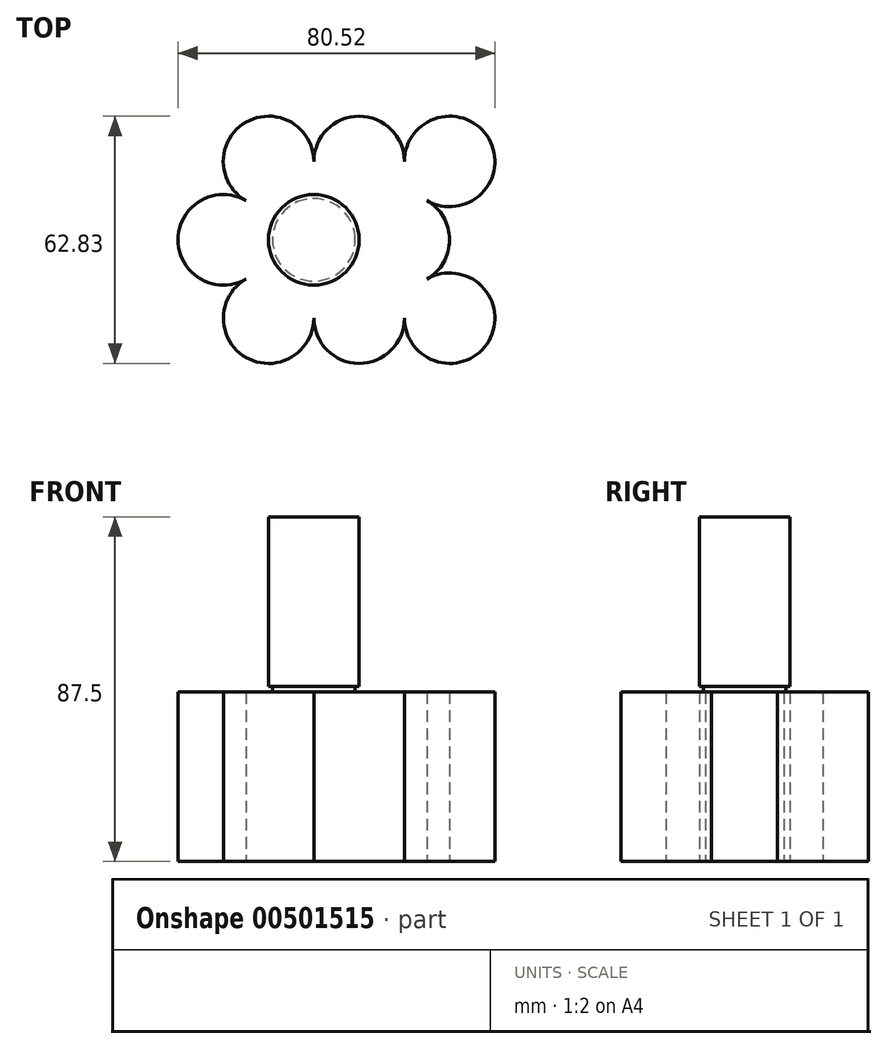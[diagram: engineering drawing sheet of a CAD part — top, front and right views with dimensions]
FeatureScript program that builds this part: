
annotation { "Feature Type Name" : "Feature", "Feature Type Description" : "" }
export const myFeature = defineFeature(function(context is Context, id is Id, definition is map)
    precondition{}
    {
        {
            var Q0;
            Q0=qCreatedBy(makeId("Top.planeOp"),FACE);
            var sketch = newSketch(context, id + "F0", { "sketchPlane" : qUnion([Q0])});
            skCircle(sketch, "E0", {"center": v(16.05, 0) * mm, "radius": 11.5 * mm});
            skPoint(sketch, "E1.first.point", {"position": v(27.55, 0) * mm});
            skCircle(sketch, "E2", {"center": v(39.05, 0) * mm, "radius": 11.5 * mm, "construction": true});
            skPoint(sketch, "E2.second.point", {"position": v(50.55, 0) * mm});
            skPoint(sketch, "E2.third.point", {"position": v(38.48, 11.49) * mm});
            skCircle(sketch, "E3", {"center": v(27.55, 19.92) * mm, "radius": 11.5 * mm});
            skPoint(sketch, "E3.first.point", {"position": v(21.8, 9.96) * mm});
            skPoint(sketch, "E3.second.point", {"position": v(33.3, 9.96) * mm});
            skPoint(sketch, "E3.third.point", {"position": v(23.6, 30.71) * mm});
            skCircle(sketch, "E4", {"center": v(27.57, -19.91) * mm, "radius": 11.5 * mm});
            skPoint(sketch, "E4.first.point", {"position": v(21.8, -9.96) * mm});
            skPoint(sketch, "E4.second.point", {"position": v(33.65, -10.15) * mm});
            skPoint(sketch, "E4.third.point", {"position": v(32.49, -30.3) * mm});
            skCircle(sketch, "E5.1.0.0", {"center": v(50.55, 19.92) * mm, "radius": 11.5 * mm});
            skCircle(sketch, "E5.1.0.1", {"center": v(39.05, 0) * mm, "radius": 11.5 * mm});
            skCircle(sketch, "E5.1.0.2", {"center": v(50.57, -19.91) * mm, "radius": 11.5 * mm});
            skCircle(sketch, "E5.2.0.0", {"center": v(73.55, 19.92) * mm, "radius": 11.5 * mm});
            skCircle(sketch, "E5.2.0.1", {"center": v(62.05, 0) * mm, "radius": 11.5 * mm});
            skCircle(sketch, "E5.2.0.2", {"center": v(73.57, -19.91) * mm, "radius": 11.5 * mm});
            skLineSegment(sketch, "E5.direction1", {"start": v(27.55, 19.92) * mm, "end": v(50.55, 19.92) * mm, "construction": true});
            skSolve(sketch);
        }
        {
            var Q0;
            Q0=qCreatedBy(makeId("Top.planeOp"),FACE);
            var sketch = newSketch(context, id + "F1", { "sketchPlane" : qUnion([Q0])});
            skCircle(sketch, "E6.0", {"center": v(27.55, 19.92) * mm, "radius": 11.5 * mm});
            skCircle(sketch, "E6.1", {"center": v(16.05, 0) * mm, "radius": 11.5 * mm});
            skCircle(sketch, "E6.2", {"center": v(27.57, -19.91) * mm, "radius": 11.5 * mm});
            skCircle(sketch, "E6.3", {"center": v(50.55, 19.92) * mm, "radius": 11.5 * mm});
            skCircle(sketch, "E6.4", {"center": v(39.05, 0) * mm, "radius": 11.5 * mm});
            skCircle(sketch, "E6.5", {"center": v(50.57, -19.91) * mm, "radius": 11.5 * mm});
            skCircle(sketch, "E6.6", {"center": v(73.55, 19.92) * mm, "radius": 11.5 * mm});
            skCircle(sketch, "E6.7", {"center": v(62.05, 0) * mm, "radius": 11.5 * mm});
            skCircle(sketch, "E6.8", {"center": v(73.57, -19.91) * mm, "radius": 11.5 * mm});
            skLineSegment(sketch, "E6.9", {"start": v(27.55, 19.92) * mm, "end": v(50.55, 19.92) * mm});
            skCircle(sketch, "E6.10", {"center": v(39.05, 0) * mm, "radius": 11.5 * mm});
            skSolve(sketch);
        }
        {
            var Q0;
            {var subQ0=sQuery(id+"F1.wireOp",EDGE,"E6.6");var subQ1=makeQuery(id+"F1.imprint","INTERSECT",VERTEX,{"derivedFrom":[sQuery(id+"F1.wireOp",EDGE,"E6.3"),subQ0]});Q0=makeQuery(id+"F1.imprint","IMPRINT",FACE,{"disambiguationData":[TD([[makeQuery(id+"F1.imprint","IMPRINT",EDGE,{"disambiguationData":[TD([[subQ1,-1.0]])],"derivedFrom":subQ0}),1.0]])]});}
            var Q1;
            {var subQ0=sQuery(id+"F1.wireOp",EDGE,"E6.8");var subQ1=makeQuery(id+"F1.imprint","INTERSECT",VERTEX,{"derivedFrom":[sQuery(id+"F1.wireOp",EDGE,"E6.5"),subQ0]});Q1=makeQuery(id+"F1.imprint","IMPRINT",FACE,{"disambiguationData":[TD([[makeQuery(id+"F1.imprint","IMPRINT",EDGE,{"disambiguationData":[TD([[subQ1,1.0]])],"derivedFrom":subQ0}),1.0]])]});}
            var Q2;
            {var subQ0=sQuery(id+"F1.wireOp",EDGE,"E6.0");var subQ1=makeQuery(id+"F1.imprint","INTERSECT",VERTEX,{"derivedFrom":[subQ0,sQuery(id+"F1.wireOp",EDGE,"E6.1")]});Q2=makeQuery(id+"F1.imprint","IMPRINT",FACE,{"disambiguationData":[TD([[makeQuery(id+"F1.imprint","IMPRINT",EDGE,{"disambiguationData":[TD([[subQ1,1.0]])],"derivedFrom":subQ0}),1.0]])]});}
            var Q3;
            {var subQ0=sQuery(id+"F1.wireOp",EDGE,"E6.1");var subQ1=makeQuery(id+"F1.imprint","INTERSECT",VERTEX,{"derivedFrom":[sQuery(id+"F1.wireOp",EDGE,"E6.0"),subQ0]});Q3=makeQuery(id+"F1.imprint","IMPRINT",FACE,{"disambiguationData":[TD([[makeQuery(id+"F1.imprint","IMPRINT",EDGE,{"disambiguationData":[TD([[subQ1,1.0]])],"derivedFrom":subQ0}),1.0]])]});}
            var Q4;
            {var subQ0=sQuery(id+"F1.wireOp",EDGE,"E6.1");var subQ1=sQuery(id+"F1.wireOp",EDGE,"E6.0");var subQ2=makeQuery(id+"F1.imprint","INTERSECT",VERTEX,{"derivedFrom":[subQ1,subQ0]});Q4=makeQuery(id+"F1.imprint","IMPRINT",FACE,{"disambiguationData":[TD([[makeQuery(id+"F1.imprint","IMPRINT",EDGE,{"disambiguationData":[TD([[subQ2,-1.0]])],"derivedFrom":subQ1}),-1.0]])]});}
            var Q5;
            {var subQ0=sQuery(id+"F1.wireOp",EDGE,"E6.3");var subQ1=sQuery(id+"F1.wireOp",EDGE,"E6.0");var subQ2=makeQuery(id+"F1.imprint","INTERSECT",VERTEX,{"derivedFrom":[subQ1,subQ0]});Q5=makeQuery(id+"F1.imprint","IMPRINT",FACE,{"disambiguationData":[TD([[makeQuery(id+"F1.imprint","IMPRINT",EDGE,{"disambiguationData":[TD([[subQ2,1.0]])],"derivedFrom":subQ1}),-1.0]])]});}
            var Q6;
            {var subQ0=sQuery(id+"F1.wireOp",EDGE,"E6.2");var subQ1=sQuery(id+"F1.wireOp",EDGE,"E6.1");var subQ2=makeQuery(id+"F1.imprint","INTERSECT",VERTEX,{"derivedFrom":[subQ1,subQ0]});Q6=makeQuery(id+"F1.imprint","IMPRINT",FACE,{"disambiguationData":[TD([[makeQuery(id+"F1.imprint","IMPRINT",EDGE,{"disambiguationData":[TD([[subQ2,-1.0]])],"derivedFrom":subQ1}),-1.0]])]});}
            var Q7;
            {var subQ0=sQuery(id+"F1.wireOp",EDGE,"E6.2");var subQ1=makeQuery(id+"F1.imprint","INTERSECT",VERTEX,{"derivedFrom":[subQ0,sQuery(id+"F1.wireOp",EDGE,"E6.5")]});Q7=makeQuery(id+"F1.imprint","IMPRINT",FACE,{"disambiguationData":[TD([[makeQuery(id+"F1.imprint","IMPRINT",EDGE,{"disambiguationData":[TD([[subQ1,-1.0]])],"derivedFrom":subQ0}),1.0]])]});}
            var Q8;
            {var subQ0=sQuery(id+"F1.wireOp",EDGE,"E6.5");var subQ1=sQuery(id+"F1.wireOp",EDGE,"E6.2");var subQ2=makeQuery(id+"F1.imprint","INTERSECT",VERTEX,{"derivedFrom":[subQ1,subQ0]});Q8=makeQuery(id+"F1.imprint","IMPRINT",FACE,{"disambiguationData":[TD([[makeQuery(id+"F1.imprint","IMPRINT",EDGE,{"disambiguationData":[TD([[subQ2,-1.0]])],"derivedFrom":subQ1}),-1.0]])]});}
            var Q9;
            {var subQ0=sQuery(id+"F1.wireOp",EDGE,"E6.3");var subQ1=makeQuery(id+"F1.imprint","INTERSECT",VERTEX,{"derivedFrom":[sQuery(id+"F1.wireOp",EDGE,"E6.0"),subQ0]});Q9=makeQuery(id+"F1.imprint","IMPRINT",FACE,{"disambiguationData":[TD([[makeQuery(id+"F1.imprint","IMPRINT",EDGE,{"disambiguationData":[TD([[subQ1,1.0]])],"derivedFrom":subQ0}),1.0]])]});}
            var Q10;
            {var subQ0=sQuery(id+"F1.wireOp",EDGE,"E6.6");var subQ1=sQuery(id+"F1.wireOp",EDGE,"E6.3");var subQ2=makeQuery(id+"F1.imprint","INTERSECT",VERTEX,{"derivedFrom":[subQ1,subQ0]});Q10=makeQuery(id+"F1.imprint","IMPRINT",FACE,{"disambiguationData":[TD([[makeQuery(id+"F1.imprint","IMPRINT",EDGE,{"disambiguationData":[TD([[subQ2,1.0]])],"derivedFrom":subQ1}),-1.0]])]});}
            var Q11;
            {var subQ0=sQuery(id+"F1.wireOp",EDGE,"E6.8");var subQ1=sQuery(id+"F1.wireOp",EDGE,"E6.5");var subQ2=makeQuery(id+"F1.imprint","INTERSECT",VERTEX,{"derivedFrom":[subQ1,subQ0]});Q11=makeQuery(id+"F1.imprint","IMPRINT",FACE,{"disambiguationData":[TD([[makeQuery(id+"F1.imprint","IMPRINT",EDGE,{"disambiguationData":[TD([[subQ2,-1.0]])],"derivedFrom":subQ1}),-1.0]])]});}
            var Q12;
            {var subQ0=sQuery(id+"F1.wireOp",EDGE,"E6.5");var subQ2=makeQuery(id+"F1.imprint","INTERSECT",VERTEX,{"derivedFrom":[subQ0,sQuery(id+"F1.wireOp",EDGE,"E6.8")]});Q12=makeQuery(id+"F1.imprint","IMPRINT",FACE,{"disambiguationData":[TD([[makeQuery(id+"F1.imprint","IMPRINT",EDGE,{"disambiguationData":[TD([[subQ2,-1.0]])],"derivedFrom":subQ0}),1.0]])]});}
            var Q13;
            {var subQ0=sQuery(id+"F1.wireOp",EDGE,"E6.7");var subQ1=sQuery(id+"F1.wireOp",EDGE,"E6.5");var subQ6=makeQuery(id+"F1.imprint","INTERSECT",VERTEX,{"disambiguationData":[OD(0.0)],"derivedFrom":[subQ1,subQ0]});Q13=makeQuery(id+"F1.imprint","IMPRINT",FACE,{"disambiguationData":[TD([[makeQuery(id+"F1.imprint","IMPRINT",EDGE,{"disambiguationData":[TD([[subQ6,-1.0]])],"derivedFrom":subQ1}),-1.0]])]});}
            var Q14;
            {var subQ0=sQuery(id+"F0.wireOp",EDGE,"E5.1.0.1");var subQ5=sQuery(id+"F0.wireOp",EDGE,"E4");var subQ6=makeQuery(id+"F0.imprint","INTERSECT",VERTEX,{"disambiguationData":[OD(0.0)],"derivedFrom":[subQ5,subQ0]});Q14=makeQuery(id+"F0.imprint","IMPRINT",FACE,{"disambiguationData":[TD([[makeQuery(id+"F0.imprint","IMPRINT",EDGE,{"disambiguationData":[TD([[subQ6,-1.0]])],"derivedFrom":subQ5}),-1.0]])]});}
            var Q15;
            {var subQ0=sQuery(id+"F0.wireOp",EDGE,"E5.2.0.2");var subQ1=sQuery(id+"F0.wireOp",EDGE,"E5.1.0.2");var subQ2=makeQuery(id+"F0.imprint","INTERSECT",VERTEX,{"derivedFrom":[subQ1,subQ0]});Q15=makeQuery(id+"F0.imprint","IMPRINT",FACE,{"disambiguationData":[TD([[makeQuery(id+"F0.imprint","IMPRINT",EDGE,{"disambiguationData":[TD([[subQ2,-1.0]])],"derivedFrom":subQ1}),-1.0]])]});}
            var Q16;
            {var subQ0=sQuery(id+"F0.wireOp",EDGE,"E5.2.0.0");var subQ1=sQuery(id+"F0.wireOp",EDGE,"E5.1.0.0");var subQ2=makeQuery(id+"F0.imprint","INTERSECT",VERTEX,{"derivedFrom":[subQ1,subQ0]});Q16=makeQuery(id+"F0.imprint","IMPRINT",FACE,{"disambiguationData":[TD([[makeQuery(id+"F0.imprint","IMPRINT",EDGE,{"disambiguationData":[TD([[subQ2,1.0]])],"derivedFrom":subQ1}),-1.0]])]});}
            var Q17;
            {var subQ0=sQuery(id+"F0.wireOp",EDGE,"E5.1.0.2");var subQ2=makeQuery(id+"F0.imprint","INTERSECT",VERTEX,{"derivedFrom":[subQ0,sQuery(id+"F0.wireOp",EDGE,"E5.2.0.2")]});Q17=makeQuery(id+"F0.imprint","IMPRINT",FACE,{"disambiguationData":[TD([[makeQuery(id+"F0.imprint","IMPRINT",EDGE,{"disambiguationData":[TD([[subQ2,-1.0]])],"derivedFrom":subQ0}),1.0]])]});}
            var Q18;
            {var subQ0=sQuery(id+"F0.wireOp",EDGE,"E5.2.0.1");var subQ2=sQuery(id+"F0.wireOp",EDGE,"E5.1.0.2");var subQ6=makeQuery(id+"F0.imprint","INTERSECT",VERTEX,{"disambiguationData":[OD(0.0)],"derivedFrom":[subQ2,subQ0]});Q18=makeQuery(id+"F0.imprint","IMPRINT",FACE,{"disambiguationData":[TD([[makeQuery(id+"F0.imprint","IMPRINT",EDGE,{"disambiguationData":[TD([[subQ6,-1.0]])],"derivedFrom":subQ2}),-1.0]])]});}
            var Q19;
            {var subQ0=sQuery(id+"F0.wireOp",EDGE,"E5.2.0.1");var subQ1=sQuery(id+"F0.wireOp",EDGE,"E5.1.0.1");var subQ2=makeQuery(id+"F0.imprint","INTERSECT",VERTEX,{"derivedFrom":[subQ1,subQ0]});Q19=makeQuery(id+"F0.imprint","IMPRINT",FACE,{"disambiguationData":[TD([[makeQuery(id+"F0.imprint","IMPRINT",EDGE,{"disambiguationData":[TD([[subQ2,1.0]])],"derivedFrom":subQ1}),-1.0]])]});}
            var Q20;
            {var subQ0=sQuery(id+"F0.wireOp",EDGE,"E5.2.0.0");var subQ1=makeQuery(id+"F0.imprint","INTERSECT",VERTEX,{"derivedFrom":[sQuery(id+"F0.wireOp",EDGE,"E5.1.0.0"),subQ0]});Q20=makeQuery(id+"F0.imprint","IMPRINT",FACE,{"disambiguationData":[TD([[makeQuery(id+"F0.imprint","IMPRINT",EDGE,{"disambiguationData":[TD([[subQ1,-1.0]])],"derivedFrom":subQ0}),1.0]])]});}
            var Q21;
            {var subQ0=sQuery(id+"F0.wireOp",EDGE,"E5.2.0.2");var subQ1=makeQuery(id+"F0.imprint","INTERSECT",VERTEX,{"derivedFrom":[sQuery(id+"F0.wireOp",EDGE,"E5.1.0.2"),subQ0]});Q21=makeQuery(id+"F0.imprint","IMPRINT",FACE,{"disambiguationData":[TD([[makeQuery(id+"F0.imprint","IMPRINT",EDGE,{"disambiguationData":[TD([[subQ1,1.0]])],"derivedFrom":subQ0}),1.0]])]});}
            var Q22;
            {var subQ0=sQuery(id+"F0.wireOp",EDGE,"E0");var subQ1=makeQuery(id+"F0.imprint","INTERSECT",VERTEX,{"derivedFrom":[subQ0,sQuery(id+"F0.wireOp",EDGE,"E3")]});Q22=makeQuery(id+"F0.imprint","IMPRINT",FACE,{"disambiguationData":[TD([[makeQuery(id+"F0.imprint","IMPRINT",EDGE,{"disambiguationData":[TD([[subQ1,1.0]])],"derivedFrom":subQ0}),1.0]])]});}
            var Q23;
            {var subQ0=sQuery(id+"F0.wireOp",EDGE,"E3");var subQ1=makeQuery(id+"F0.imprint","INTERSECT",VERTEX,{"derivedFrom":[sQuery(id+"F0.wireOp",EDGE,"E0"),subQ0]});Q23=makeQuery(id+"F0.imprint","IMPRINT",FACE,{"disambiguationData":[TD([[makeQuery(id+"F0.imprint","IMPRINT",EDGE,{"disambiguationData":[TD([[subQ1,1.0]])],"derivedFrom":subQ0}),1.0]])]});}
            var Q24;
            {var subQ0=sQuery(id+"F0.wireOp",EDGE,"E3");var subQ1=sQuery(id+"F0.wireOp",EDGE,"E0");var subQ2=makeQuery(id+"F0.imprint","INTERSECT",VERTEX,{"derivedFrom":[subQ1,subQ0]});Q24=makeQuery(id+"F0.imprint","IMPRINT",FACE,{"disambiguationData":[TD([[makeQuery(id+"F0.imprint","IMPRINT",EDGE,{"disambiguationData":[TD([[subQ2,1.0]])],"derivedFrom":subQ1}),-1.0]])]});}
            var Q25;
            {var subQ0=sQuery(id+"F0.wireOp",EDGE,"E4");var subQ1=sQuery(id+"F0.wireOp",EDGE,"E0");var subQ2=makeQuery(id+"F0.imprint","INTERSECT",VERTEX,{"derivedFrom":[subQ1,subQ0]});Q25=makeQuery(id+"F0.imprint","IMPRINT",FACE,{"disambiguationData":[TD([[makeQuery(id+"F0.imprint","IMPRINT",EDGE,{"disambiguationData":[TD([[subQ2,-1.0]])],"derivedFrom":subQ1}),-1.0]])]});}
            var Q26;
            {var subQ0=sQuery(id+"F0.wireOp",EDGE,"E5.1.0.0");var subQ1=sQuery(id+"F0.wireOp",EDGE,"E3");var subQ2=makeQuery(id+"F0.imprint","INTERSECT",VERTEX,{"derivedFrom":[subQ1,subQ0]});Q26=makeQuery(id+"F0.imprint","IMPRINT",FACE,{"disambiguationData":[TD([[makeQuery(id+"F0.imprint","IMPRINT",EDGE,{"disambiguationData":[TD([[subQ2,1.0]])],"derivedFrom":subQ1}),-1.0]])]});}
            var Q27;
            {var subQ0=sQuery(id+"F0.wireOp",EDGE,"E4");var subQ1=makeQuery(id+"F0.imprint","INTERSECT",VERTEX,{"derivedFrom":[subQ0,sQuery(id+"F0.wireOp",EDGE,"E5.1.0.2")]});Q27=makeQuery(id+"F0.imprint","IMPRINT",FACE,{"disambiguationData":[TD([[makeQuery(id+"F0.imprint","IMPRINT",EDGE,{"disambiguationData":[TD([[subQ1,-1.0]])],"derivedFrom":subQ0}),1.0]])]});}
            var Q28;
            {var subQ0=sQuery(id+"F0.wireOp",EDGE,"E5.1.0.2");var subQ1=sQuery(id+"F0.wireOp",EDGE,"E4");var subQ2=makeQuery(id+"F0.imprint","INTERSECT",VERTEX,{"derivedFrom":[subQ1,subQ0]});Q28=makeQuery(id+"F0.imprint","IMPRINT",FACE,{"disambiguationData":[TD([[makeQuery(id+"F0.imprint","IMPRINT",EDGE,{"disambiguationData":[TD([[subQ2,-1.0]])],"derivedFrom":subQ1}),-1.0]])]});}
            var Q29;
            {var subQ0=sQuery(id+"F0.wireOp",EDGE,"E5.1.0.0");var subQ1=makeQuery(id+"F0.imprint","INTERSECT",VERTEX,{"derivedFrom":[sQuery(id+"F0.wireOp",EDGE,"E3"),subQ0]});Q29=makeQuery(id+"F0.imprint","IMPRINT",FACE,{"disambiguationData":[TD([[makeQuery(id+"F0.imprint","IMPRINT",EDGE,{"disambiguationData":[TD([[subQ1,1.0]])],"derivedFrom":subQ0}),1.0]])]});}
            var Q30;
            {var subQ0=sQuery(id+"F0.wireOp",EDGE,"E5.1.0.1");var subQ1=sQuery(id+"F0.wireOp",EDGE,"E5.1.0.0");var subQ2=makeQuery(id+"F0.imprint","INTERSECT",VERTEX,{"derivedFrom":[subQ1,subQ0]});Q30=makeQuery(id+"F0.imprint","IMPRINT",FACE,{"disambiguationData":[TD([[makeQuery(id+"F0.imprint","IMPRINT",EDGE,{"disambiguationData":[TD([[subQ2,-1.0]])],"derivedFrom":subQ1}),-1.0]])]});}
            var Q31;
            {var subQ0=sQuery(id+"F1.wireOp",EDGE,"E6.10");var subQ5=sQuery(id+"F1.wireOp",EDGE,"E6.2");var subQ6=makeQuery(id+"F1.imprint","INTERSECT",VERTEX,{"disambiguationData":[OD(0.0)],"derivedFrom":[subQ5,subQ0]});Q31=makeQuery(id+"F1.imprint","IMPRINT",FACE,{"disambiguationData":[TD([[makeQuery(id+"F1.imprint","IMPRINT",EDGE,{"disambiguationData":[TD([[subQ6,-1.0]])],"derivedFrom":subQ5}),-1.0]])]});}
            var Q32;
            {var subQ0=sQuery(id+"F1.wireOp",EDGE,"E6.10");var subQ1=sQuery(id+"F1.wireOp",EDGE,"E6.3");var subQ2=makeQuery(id+"F1.imprint","INTERSECT",VERTEX,{"derivedFrom":[subQ1,subQ0]});Q32=makeQuery(id+"F1.imprint","IMPRINT",FACE,{"disambiguationData":[TD([[makeQuery(id+"F1.imprint","IMPRINT",EDGE,{"disambiguationData":[TD([[subQ2,-1.0]])],"derivedFrom":subQ1}),-1.0]])]});}
            var Q33;
            {var subQ0=sQuery(id+"F1.wireOp",EDGE,"E6.7");var subQ1=sQuery(id+"F1.wireOp",EDGE,"E6.5");var subQ2=makeQuery(id+"F1.imprint","INTERSECT",VERTEX,{"disambiguationData":[OD(1.0)],"derivedFrom":[subQ1,subQ0]});Q33=makeQuery(id+"F1.imprint","IMPRINT",FACE,{"disambiguationData":[TD([[makeQuery(id+"F1.imprint","IMPRINT",EDGE,{"disambiguationData":[TD([[subQ2,-1.0]])],"derivedFrom":subQ1}),-1.0]])]});}
            var Q34;
            {var subQ0=sQuery(id+"F0.wireOp",EDGE,"E5.2.0.1");var subQ1=sQuery(id+"F0.wireOp",EDGE,"E5.1.0.2");var subQ2=makeQuery(id+"F0.imprint","INTERSECT",VERTEX,{"disambiguationData":[OD(0.0)],"derivedFrom":[subQ1,subQ0]});Q34=makeQuery(id+"F0.imprint","IMPRINT",FACE,{"disambiguationData":[TD([[makeQuery(id+"F0.imprint","IMPRINT",EDGE,{"disambiguationData":[TD([[subQ2,-1.0]])],"derivedFrom":subQ1}),1.0]])]});}
            var Q35;
            {var subQ0=sQuery(id+"F1.wireOp",EDGE,"E6.7");var subQ1=sQuery(id+"F1.wireOp",EDGE,"E6.5");var subQ2=makeQuery(id+"F1.imprint","INTERSECT",VERTEX,{"disambiguationData":[OD(0.0)],"derivedFrom":[subQ1,subQ0]});Q35=makeQuery(id+"F1.imprint","IMPRINT",FACE,{"disambiguationData":[TD([[makeQuery(id+"F1.imprint","IMPRINT",EDGE,{"disambiguationData":[TD([[subQ2,-1.0]])],"derivedFrom":subQ1}),1.0]])]});}
            var Q36;
            {var subQ0=sQuery(id+"F0.wireOp",EDGE,"E5.1.0.1");var subQ1=sQuery(id+"F0.wireOp",EDGE,"E4");var subQ2=makeQuery(id+"F0.imprint","INTERSECT",VERTEX,{"disambiguationData":[OD(0.0)],"derivedFrom":[subQ1,subQ0]});Q36=makeQuery(id+"F0.imprint","IMPRINT",FACE,{"disambiguationData":[TD([[makeQuery(id+"F0.imprint","IMPRINT",EDGE,{"disambiguationData":[TD([[subQ2,-1.0]])],"derivedFrom":subQ1}),1.0]])]});}
            var Q37;
            {var subQ0=sQuery(id+"F1.wireOp",EDGE,"E6.10");var subQ1=sQuery(id+"F1.wireOp",EDGE,"E6.2");var subQ2=makeQuery(id+"F1.imprint","INTERSECT",VERTEX,{"disambiguationData":[OD(0.0)],"derivedFrom":[subQ1,subQ0]});Q37=makeQuery(id+"F1.imprint","IMPRINT",FACE,{"disambiguationData":[TD([[makeQuery(id+"F1.imprint","IMPRINT",EDGE,{"disambiguationData":[TD([[subQ2,-1.0]])],"derivedFrom":subQ1}),1.0]])]});}
            extrude(context, id + "F2", {"entities" : qUnion([Q0, Q1, Q2, Q3, Q4, Q5, Q6, Q7, Q8, Q9, Q10, Q11, Q12, Q13, Q14, Q15, Q16, Q17, Q18, Q19, Q20, Q21, Q22, Q23, Q24, Q25, Q26, Q27, Q28, Q29, Q30, Q31, Q32, Q33, Q34, Q35, Q36, Q37]), "depth" : 43 * mm});
        }
        {
            var Q0;
            Q0=qCreatedBy(makeId("Top.planeOp"),FACE);
            cPlane(context, id + "F3", {"entities" : qUnion([Q0]), "cplaneType" : CPlaneType.OFFSET, "offset" : 43 * mm, "width" : 150 * mm, "height" : 150 * mm});
        }
        {
            var Q0;
            Q0=qCreatedBy(id+"F3.planeOp",FACE);
            var sketch = newSketch(context, id + "F4", { "sketchPlane" : qUnion([Q0])});
            skLineSegment(sketch, "E7", {"start": v(39.05, 21.56) * mm, "end": v(39.05, -21.56) * mm, "construction": true});
            skPoint(sketch, "E8", {"position": v(39.05, 0) * mm});
            skPoint(sketch, "E8.positionSnap0", {"position": v(39.05, 0) * mm});
            skCircle(sketch, "E9", {"center": v(39.05, 0) * mm, "radius": 10.5 * mm});
            skSolve(sketch);
        }
        {
            var Q0;
            Q0 = qSketchRegion(id + "F4", true);
            extrude(context, id + "F5", {"entities" : qUnion([Q0]), "depth" : 1.5 * mm});
        }
        {
            var Q0;
            Q0=qCreatedBy(makeId("Top.planeOp"),FACE);
            cPlane(context, id + "F6", {"entities" : qUnion([Q0]), "cplaneType" : CPlaneType.OFFSET, "offset" : 44.5 * mm, "width" : 150 * mm, "height" : 150 * mm});
        }
        {
            var Q0;
            Q0=qCreatedBy(id+"F6.planeOp",FACE);
            var sketch = newSketch(context, id + "F7", { "sketchPlane" : qUnion([Q0])});
            skCircle(sketch, "E10.0", {"center": v(39.05, 0) * mm, "radius": 10.5 * mm});
            skCircle(sketch, "E11", {"center": v(39.05, 0) * mm, "radius": 11.5 * mm});
            skSolve(sketch);
        }
        {
            var Q0;
            Q0=qCreatedBy(id+"F6.planeOp",FACE);
            var sketch = newSketch(context, id + "F8", { "sketchPlane" : qUnion([Q0])});
            skCircle(sketch, "E12.0", {"center": v(39.05, 0) * mm, "radius": 11.5 * mm});
            skSolve(sketch);
        }
        {
            var Q0;
            Q0 = qSketchRegion(id + "F8", true);
            extrude(context, id + "F9", {"entities" : qUnion([Q0]), "depth" : 43 * mm});
        }
    });
